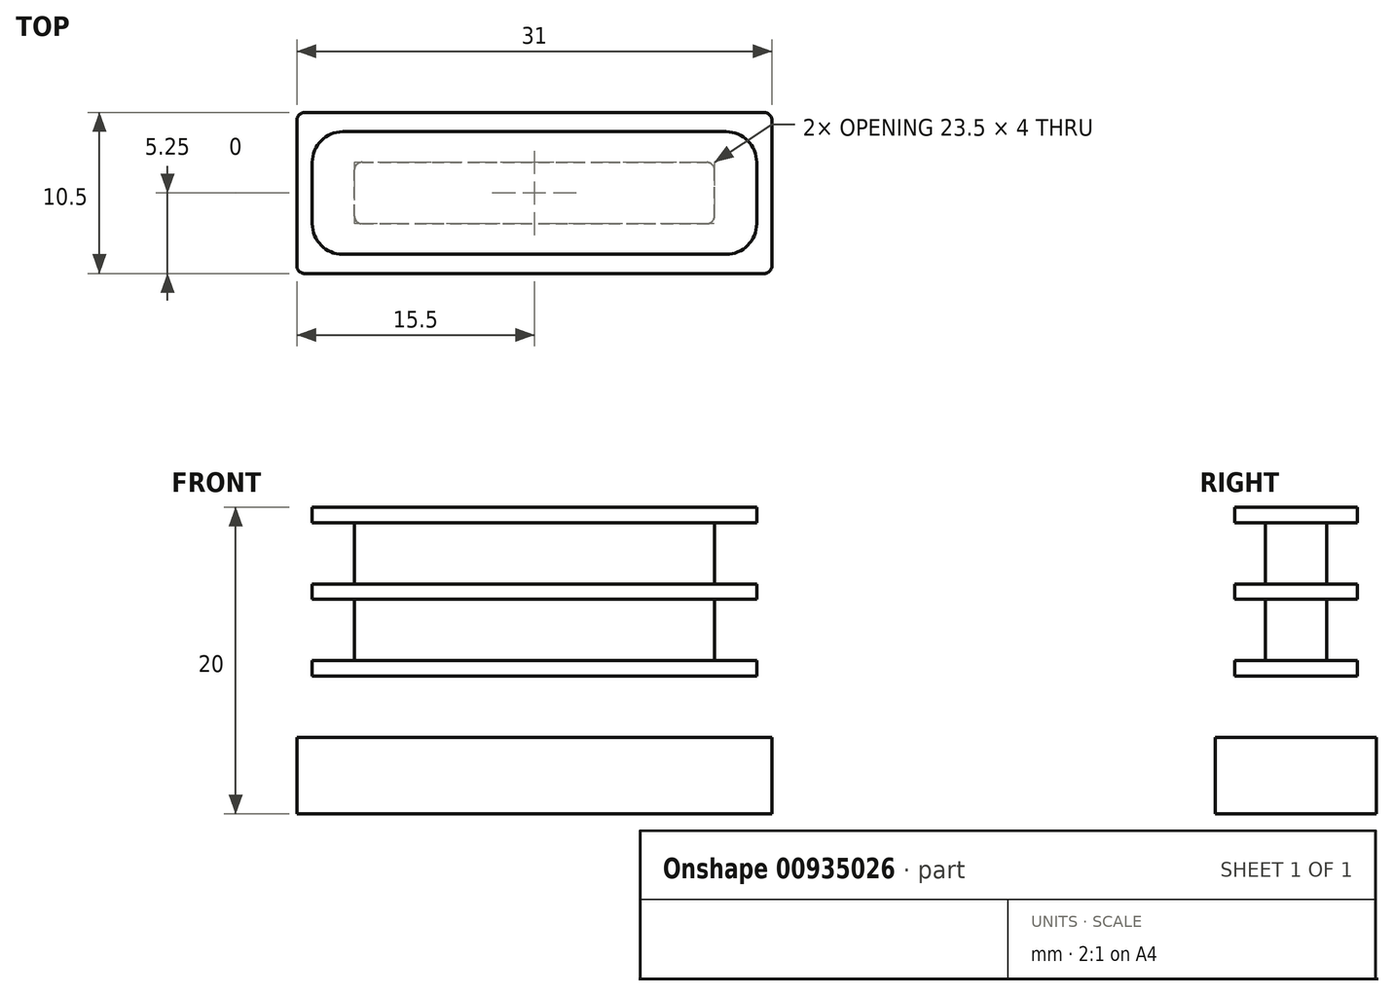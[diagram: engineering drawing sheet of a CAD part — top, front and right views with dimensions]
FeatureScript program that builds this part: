
annotation { "Feature Type Name" : "Feature", "Feature Type Description" : "" }
export const myFeature = defineFeature(function(context is Context, id is Id, definition is map)
    precondition{}
    {
        {
            var Q0;
            Q0=qCreatedBy(makeId("Front.planeOp"),FACE);
            var sketch = newSketch(context, id + "F0", { "sketchPlane" : qUnion([Q0])});
            skLineSegment(sketch, "E0.bottom", {"start": v(-15.5, 0) * mm, "end": v(15.5, 0) * mm});
            skLineSegment(sketch, "E0.top", {"start": v(-15.5, -5) * mm, "end": v(15.5, -5) * mm});
            skLineSegment(sketch, "E0.left", {"start": v(-15.5, 0) * mm, "end": v(-15.5, -5) * mm});
            skLineSegment(sketch, "E0.right", {"start": v(15.5, 0) * mm, "end": v(15.5, -5) * mm});
            skLineSegment(sketch, "E1.bottom", {"start": v(-11.75, 4) * mm, "end": v(11.75, 4) * mm});
            skLineSegment(sketch, "E1.top", {"start": v(-11.75, 0) * mm, "end": v(11.75, 0) * mm});
            skLineSegment(sketch, "E1.left", {"start": v(-11.75, 4) * mm, "end": v(-11.75, 0) * mm});
            skLineSegment(sketch, "E1.right", {"start": v(11.75, 4) * mm, "end": v(11.75, 0) * mm});
            skLineSegment(sketch, "E2.bottom", {"start": v(-14.5, 5) * mm, "end": v(14.5, 5) * mm});
            skLineSegment(sketch, "E2.top", {"start": v(-14.5, 4) * mm, "end": v(14.5, 4) * mm});
            skLineSegment(sketch, "E2.left", {"start": v(-14.5, 5) * mm, "end": v(-14.5, 4) * mm});
            skLineSegment(sketch, "E2.right", {"start": v(14.5, 5) * mm, "end": v(14.5, 4) * mm});
            skLineSegment(sketch, "E3.0.1.0", {"start": v(-11.75, 9) * mm, "end": v(-11.75, 5) * mm});
            skLineSegment(sketch, "E3.0.1.1", {"start": v(-14.5, 9) * mm, "end": v(14.5, 9) * mm});
            skLineSegment(sketch, "E3.0.1.2", {"start": v(-14.5, 10) * mm, "end": v(-14.5, 9) * mm});
            skLineSegment(sketch, "E3.0.1.3", {"start": v(-14.5, 10) * mm, "end": v(14.5, 10) * mm});
            skLineSegment(sketch, "E3.0.1.4", {"start": v(14.5, 10) * mm, "end": v(14.5, 9) * mm});
            skLineSegment(sketch, "E3.0.1.5", {"start": v(11.75, 9) * mm, "end": v(11.75, 5) * mm});
            skLineSegment(sketch, "E3.0.2.0", {"start": v(-11.75, 14) * mm, "end": v(-11.75, 10) * mm});
            skLineSegment(sketch, "E3.0.2.1", {"start": v(-14.5, 14) * mm, "end": v(14.5, 14) * mm});
            skLineSegment(sketch, "E3.0.2.2", {"start": v(-14.5, 15) * mm, "end": v(-14.5, 14) * mm});
            skLineSegment(sketch, "E3.0.2.3", {"start": v(-14.5, 15) * mm, "end": v(14.5, 15) * mm});
            skLineSegment(sketch, "E3.0.2.4", {"start": v(14.5, 15) * mm, "end": v(14.5, 14) * mm});
            skLineSegment(sketch, "E3.0.2.5", {"start": v(11.75, 14) * mm, "end": v(11.75, 10) * mm});
            skLineSegment(sketch, "E3.direction1", {"start": v(-11.75, 0) * mm, "end": v(13.25, 0) * mm, "construction": true});
            skLineSegment(sketch, "E3.direction2", {"start": v(-11.75, 0) * mm, "end": v(-11.75, 5) * mm, "construction": true});
            skSolve(sketch);
        }
        {
            var Q0;
            Q0=makeQuery(id+"F0.imprint","IMPRINT",FACE,{"disambiguationData":[TD([[makeQuery(id+"F0.imprint","IMPRINT",EDGE,{"derivedFrom":sQuery(id+"F0.wireOp",EDGE,"E0.top")}),1.0]])]});
            extrude(context, id + "F1", {"entities" : qUnion([Q0]), "endBound" : BoundingType.SYMMETRIC, "depth" : 10.5 * mm, "offsetDistance" : 25 * mm});
        }
        {
            var Q0;
            {var subQ2=sQuery(id+"F0.wireOp",EDGE,"E2.left");Q0=makeQuery(id+"F0.imprint","IMPRINT",FACE,{"disambiguationData":[TD([[makeQuery(id+"F0.imprint","IMPRINT",EDGE,{"derivedFrom":subQ2}),1.0]])]});}
            var Q1;
            {var subQ0=sQuery(id+"F0.wireOp",EDGE,"E3.0.1.2");Q1=makeQuery(id+"F0.imprint","IMPRINT",FACE,{"disambiguationData":[TD([[makeQuery(id+"F0.imprint","IMPRINT",EDGE,{"derivedFrom":subQ0}),1.0]])]});}
            var Q2;
            {var subQ0=sQuery(id+"F0.wireOp",EDGE,"E3.0.2.2");Q2=makeQuery(id+"F0.imprint","IMPRINT",FACE,{"disambiguationData":[TD([[makeQuery(id+"F0.imprint","IMPRINT",EDGE,{"derivedFrom":subQ0}),1.0]])]});}
            extrude(context, id + "F2", {"entities" : qUnion([Q0, Q1, Q2]), "endBound" : BoundingType.SYMMETRIC, "depth" : 8 * mm, "offsetDistance" : 25 * mm});
        }
        {
            var Q0;
            Q0=makeQuery(id+"F0.imprint","IMPRINT",FACE,{"disambiguationData":[TD([[makeQuery(id+"F0.imprint","IMPRINT",EDGE,{"derivedFrom":sQuery(id+"F0.wireOp",EDGE,"E1.top")}),1.0]])]});
            var Q1;
            {var subQ0=sQuery(id+"F0.wireOp",EDGE,"E3.0.1.0");Q1=makeQuery(id+"F0.imprint","IMPRINT",FACE,{"disambiguationData":[TD([[makeQuery(id+"F0.imprint","IMPRINT",EDGE,{"derivedFrom":subQ0}),1.0]])]});}
            var Q2;
            {var subQ0=sQuery(id+"F0.wireOp",EDGE,"E3.0.2.0");Q2=makeQuery(id+"F0.imprint","IMPRINT",FACE,{"disambiguationData":[TD([[makeQuery(id+"F0.imprint","IMPRINT",EDGE,{"derivedFrom":subQ0}),1.0]])]});}
            extrude(context, id + "F3", {"entities" : qUnion([Q0, Q1, Q2]), "operationType" : NewBodyOperationType.ADD, "endBound" : BoundingType.SYMMETRIC, "depth" : 4 * mm, "offsetDistance" : 25 * mm});
        }
        {
            var Q0;
            Q0=makeQuery(id+"F1.opExtrude","CAP_EDGE",EDGE,{"disambiguationData":[OSD([sQuery(id+"F0.wireOp",EDGE,"E0.right")])],"isStart":false});
            var Q1;
            Q1=makeQuery(id+"F1.opExtrude","CAP_EDGE",EDGE,{"disambiguationData":[OSD([sQuery(id+"F0.wireOp",EDGE,"E0.right")])],"isStart":true});
            var Q2;
            Q2=makeQuery(id+"F1.opExtrude","CAP_EDGE",EDGE,{"disambiguationData":[OSD([sQuery(id+"F0.wireOp",EDGE,"E0.left")])],"isStart":false});
            var Q3;
            Q3=makeQuery(id+"F3.opExtrude","CAP_EDGE",EDGE,{"disambiguationData":[OSD([sQuery(id+"F0.wireOp",EDGE,"E1.left")])],"isStart":false});
            var Q4;
            Q4=makeQuery(id+"F3.opExtrude","CAP_EDGE",EDGE,{"disambiguationData":[OSD([sQuery(id+"F0.wireOp",EDGE,"E3.0.1.0")])],"isStart":false});
            var Q5;
            Q5=makeQuery(id+"F3.opExtrude","CAP_EDGE",EDGE,{"disambiguationData":[OSD([sQuery(id+"F0.wireOp",EDGE,"E3.0.2.0")])],"isStart":false});
            var Q6;
            Q6=makeQuery(id+"F3.opExtrude","CAP_EDGE",EDGE,{"disambiguationData":[OSD([sQuery(id+"F0.wireOp",EDGE,"E1.right")])],"isStart":false});
            var Q7;
            Q7=makeQuery(id+"F3.opExtrude","CAP_EDGE",EDGE,{"disambiguationData":[OSD([sQuery(id+"F0.wireOp",EDGE,"E3.0.1.5")])],"isStart":false});
            var Q8;
            Q8=makeQuery(id+"F3.opExtrude","CAP_EDGE",EDGE,{"disambiguationData":[OSD([sQuery(id+"F0.wireOp",EDGE,"E3.0.2.5")])],"isStart":false});
            var Q9;
            Q9=makeQuery(id+"F3.opExtrude","CAP_EDGE",EDGE,{"disambiguationData":[OSD([sQuery(id+"F0.wireOp",EDGE,"E1.right")])],"isStart":true});
            var Q10;
            Q10=makeQuery(id+"F3.opExtrude","CAP_EDGE",EDGE,{"disambiguationData":[OSD([sQuery(id+"F0.wireOp",EDGE,"E3.0.1.5")])],"isStart":true});
            var Q11;
            Q11=makeQuery(id+"F3.opExtrude","CAP_EDGE",EDGE,{"disambiguationData":[OSD([sQuery(id+"F0.wireOp",EDGE,"E3.0.2.5")])],"isStart":true});
            var Q12;
            Q12=makeQuery(id+"F1.opExtrude","CAP_EDGE",EDGE,{"disambiguationData":[OSD([sQuery(id+"F0.wireOp",EDGE,"E0.left")])],"isStart":true});
            var Q13;
            Q13=makeQuery(id+"F3.opExtrude","CAP_EDGE",EDGE,{"disambiguationData":[OSD([sQuery(id+"F0.wireOp",EDGE,"E1.left")])],"isStart":true});
            var Q14;
            Q14=makeQuery(id+"F3.opExtrude","CAP_EDGE",EDGE,{"disambiguationData":[OSD([sQuery(id+"F0.wireOp",EDGE,"E3.0.1.0")])],"isStart":true});
            var Q15;
            Q15=makeQuery(id+"F3.opExtrude","CAP_EDGE",EDGE,{"disambiguationData":[OSD([sQuery(id+"F0.wireOp",EDGE,"E3.0.2.0")])],"isStart":true});
            fillet(context, id + "F4", {"entities" : qUnion([Q0, Q1, Q2, Q3, Q4, Q5, Q6, Q7, Q8, Q9, Q10, Q11, Q12, Q13, Q14, Q15]), "radius" : 0.5 * mm, "tangentPropagation" : true, "allowEdgeOverflow" : false});
        }
        {
            var Q0;
            Q0=makeQuery(id+"F2.opExtrude","CAP_EDGE",EDGE,{"disambiguationData":[OSD([sQuery(id+"F0.wireOp",EDGE,"E2.left")])],"isStart":true});
            var Q1;
            Q1=makeQuery(id+"F2.opExtrude","CAP_EDGE",EDGE,{"disambiguationData":[OSD([sQuery(id+"F0.wireOp",EDGE,"E3.0.1.2")])],"isStart":true});
            var Q2;
            Q2=makeQuery(id+"F2.opExtrude","CAP_EDGE",EDGE,{"disambiguationData":[OSD([sQuery(id+"F0.wireOp",EDGE,"E3.0.2.2")])],"isStart":true});
            var Q3;
            Q3=makeQuery(id+"F2.opExtrude","CAP_EDGE",EDGE,{"disambiguationData":[OSD([sQuery(id+"F0.wireOp",EDGE,"E3.0.2.2")])],"isStart":false});
            var Q4;
            Q4=makeQuery(id+"F2.opExtrude","CAP_EDGE",EDGE,{"disambiguationData":[OSD([sQuery(id+"F0.wireOp",EDGE,"E3.0.1.2")])],"isStart":false});
            var Q5;
            Q5=makeQuery(id+"F2.opExtrude","CAP_EDGE",EDGE,{"disambiguationData":[OSD([sQuery(id+"F0.wireOp",EDGE,"E2.left")])],"isStart":false});
            var Q6;
            Q6=makeQuery(id+"F2.opExtrude","CAP_EDGE",EDGE,{"disambiguationData":[OSD([sQuery(id+"F0.wireOp",EDGE,"E3.0.2.4")])],"isStart":false});
            var Q7;
            Q7=makeQuery(id+"F2.opExtrude","CAP_EDGE",EDGE,{"disambiguationData":[OSD([sQuery(id+"F0.wireOp",EDGE,"E3.0.1.4")])],"isStart":false});
            var Q8;
            Q8=makeQuery(id+"F2.opExtrude","CAP_EDGE",EDGE,{"disambiguationData":[OSD([sQuery(id+"F0.wireOp",EDGE,"E2.right")])],"isStart":false});
            var Q9;
            Q9=makeQuery(id+"F2.opExtrude","CAP_EDGE",EDGE,{"disambiguationData":[OSD([sQuery(id+"F0.wireOp",EDGE,"E2.right")])],"isStart":true});
            var Q10;
            Q10=makeQuery(id+"F2.opExtrude","CAP_EDGE",EDGE,{"disambiguationData":[OSD([sQuery(id+"F0.wireOp",EDGE,"E3.0.1.4")])],"isStart":true});
            var Q11;
            Q11=makeQuery(id+"F2.opExtrude","CAP_EDGE",EDGE,{"disambiguationData":[OSD([sQuery(id+"F0.wireOp",EDGE,"E3.0.2.4")])],"isStart":true});
            fillet(context, id + "F5", {"entities" : qUnion([Q0, Q1, Q2, Q3, Q4, Q5, Q6, Q7, Q8, Q9, Q10, Q11]), "radius" : 2 * mm, "tangentPropagation" : true, "allowEdgeOverflow" : false});
        }
    });
